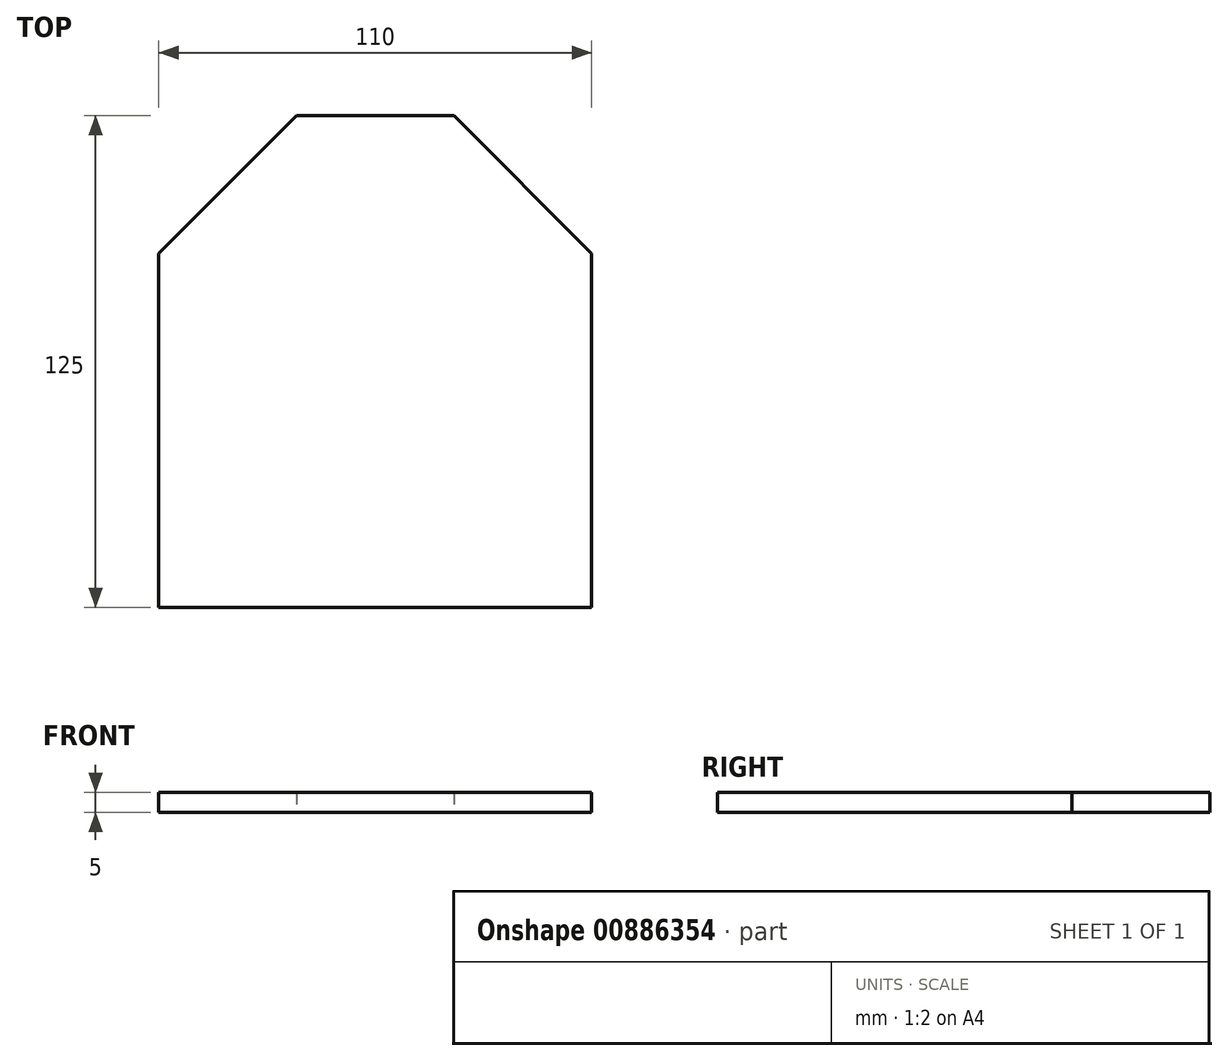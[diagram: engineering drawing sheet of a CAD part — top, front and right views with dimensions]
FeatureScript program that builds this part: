
annotation { "Feature Type Name" : "Feature", "Feature Type Description" : "" }
export const myFeature = defineFeature(function(context is Context, id is Id, definition is map)
    precondition{}
    {
        {
            var Q0;
            Q0=qCreatedBy(makeId("Top.planeOp"),FACE);
            var sketch = newSketch(context, id + "F0", { "sketchPlane" : qUnion([Q0])});
            skLineSegment(sketch, "E0", {"start": v(0, 62.5) * mm, "end": v(0, -62.5) * mm, "construction": true});
            skLineSegment(sketch, "E1", {"start": v(-55, 0) * mm, "end": v(55, 0) * mm, "construction": true});
            skLineSegment(sketch, "E2.bottom", {"start": v(-20, 62.5) * mm, "end": v(55, 62.5) * mm});
            skLineSegment(sketch, "E2.top", {"start": v(-55, -62.5) * mm, "end": v(55, -62.5) * mm});
            skLineSegment(sketch, "E2.left", {"start": v(-55, 27.5) * mm, "end": v(-55, -62.5) * mm});
            skLineSegment(sketch, "E2.right", {"start": v(55, 62.5) * mm, "end": v(55, -62.5) * mm});
            skLineSegment(sketch, "E3", {"start": v(-55, 27.5) * mm, "end": v(-20, 62.5) * mm});
            skLineSegment(sketch, "E4.MirrorCS", {"start": v(55, 27.5) * mm, "end": v(20, 62.5) * mm});
            skPoint(sketch, "E5.orphan", {"position": v(-55, 62.5) * mm});
            skSolve(sketch);
        }
        {
            var Q0;
            {var subQ0=sQuery(id+"F0.wireOp",EDGE,"E2.top");Q0=makeQuery(id+"F0.imprint","IMPRINT",FACE,{"disambiguationData":[TD([[makeQuery(id+"F0.imprint","IMPRINT",EDGE,{"derivedFrom":subQ0}),1.0]])]});}
            extrude(context, id + "F1", {"entities" : qUnion([Q0]), "depth" : 5 * mm, "offsetDistance" : 25 * mm});
        }
    });
